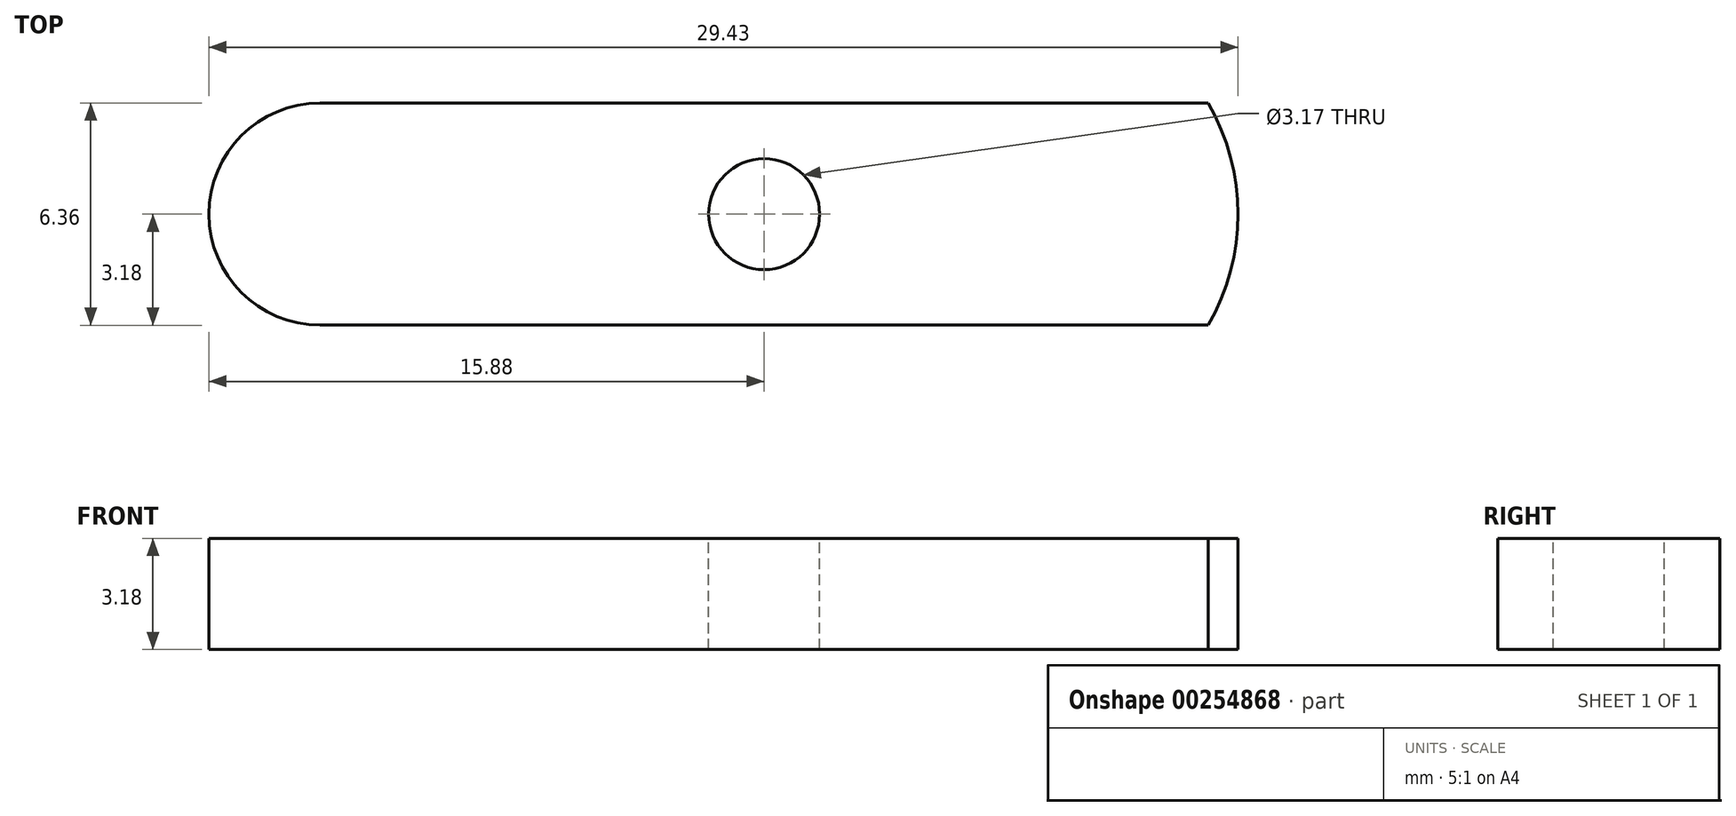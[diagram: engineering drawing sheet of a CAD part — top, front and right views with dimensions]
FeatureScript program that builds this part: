
annotation { "Feature Type Name" : "Feature", "Feature Type Description" : "" }
export const myFeature = defineFeature(function(context is Context, id is Id, definition is map)
    precondition{}
    {
        {
            var Q0;
            Q0=qCreatedBy(makeId("Top.planeOp"),FACE);
            var sketch = newSketch(context, id + "F0", { "sketchPlane" : qUnion([Q0])});
            skCircle(sketch, "E0", {"center": v(0, 0) * mm, "radius": 1.59 * mm});
            skLineSegment(sketch, "E1.bottom", {"start": v(12.7, 3.17) * mm, "end": v(-12.7, 3.17) * mm});
            skLineSegment(sketch, "E1.top", {"start": v(12.7, -3.18) * mm, "end": v(-12.7, -3.18) * mm});
            skArc(sketch, "E2", {"start": v(-12.7, 3.18) * mm, "mid": v(-15.88, 0) * mm, "end": v(-12.7, -3.18) * mm});
            skArc(sketch, "E3", {"start": v(12.7, -3.18) * mm, "mid": v(13.55, 0) * mm, "end": v(12.7, 3.17) * mm});
            skSolve(sketch);
        }
        {
            var Q0;
            Q0 = qSketchRegion(id + "F0", true);
            extrude(context, id + "F1", {"entities" : qUnion([Q0]), "oppositeDirection" : true, "depth" : 3.17 * mm});
        }
    });
